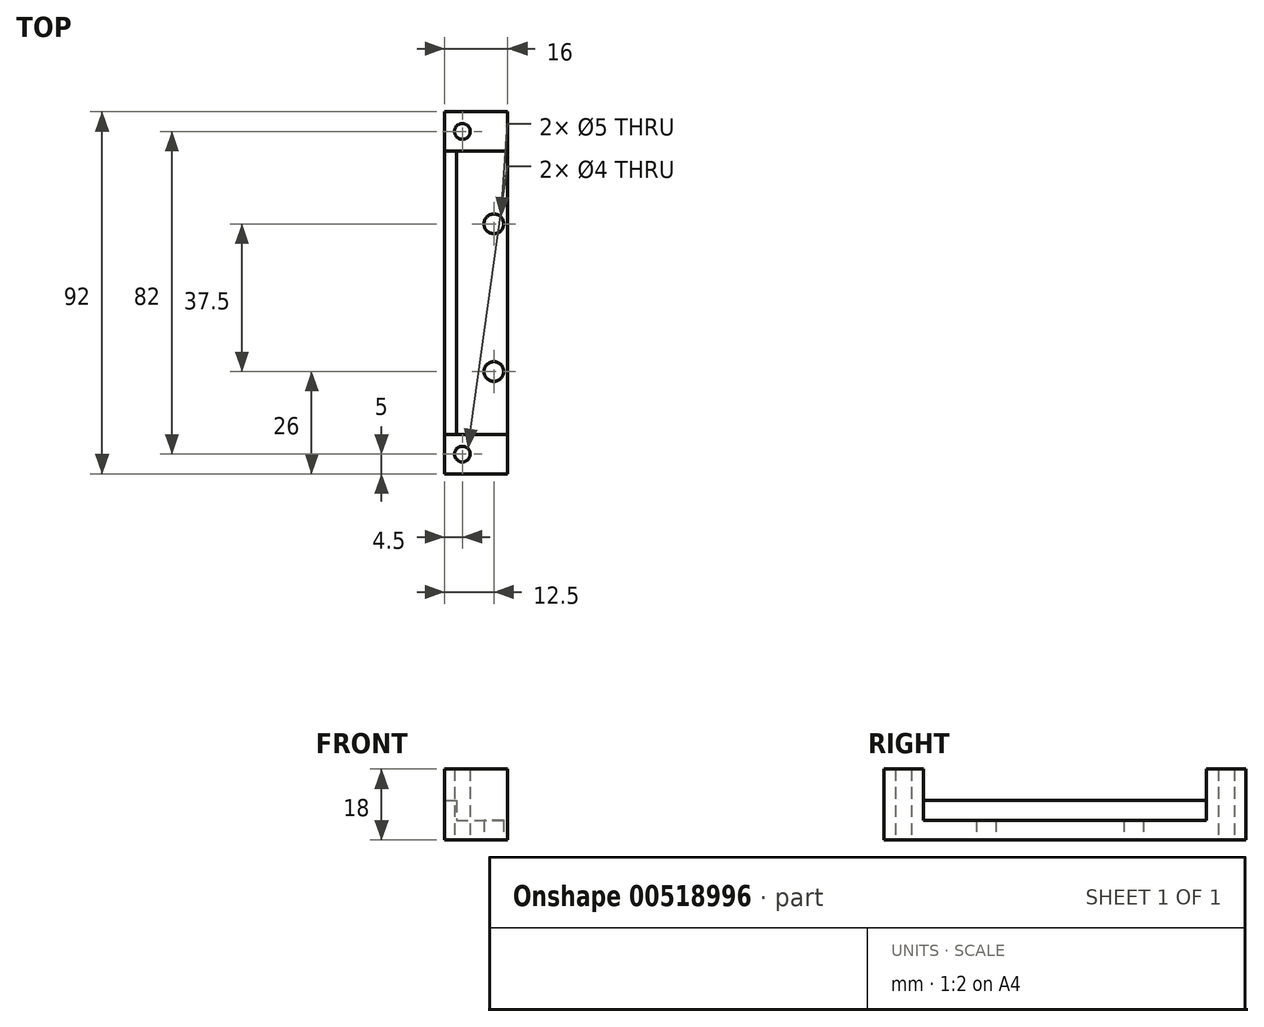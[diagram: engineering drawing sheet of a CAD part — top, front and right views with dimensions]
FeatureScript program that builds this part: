
annotation { "Feature Type Name" : "Feature", "Feature Type Description" : "" }
export const myFeature = defineFeature(function(context is Context, id is Id, definition is map)
    precondition{}
    {
        {
            var Q0;
            Q0=qCreatedBy(makeId("Top.planeOp"),FACE);
            var sketch = newSketch(context, id + "F0", { "sketchPlane" : qUnion([Q0])});
            skLineSegment(sketch, "E0.bottom", {"start": v(8, -46) * mm, "end": v(-8, -46) * mm});
            skLineSegment(sketch, "E0.top", {"start": v(8, 46) * mm, "end": v(-8, 46) * mm});
            skLineSegment(sketch, "E0.left", {"start": v(8, -46) * mm, "end": v(8, 46) * mm});
            skLineSegment(sketch, "E0.right", {"start": v(-8, -46) * mm, "end": v(-8, 46) * mm});
            skPoint(sketch, "E0.middle", {"position": v(0, 0) * mm});
            skCircle(sketch, "E1", {"center": v(4.5, 17.5) * mm, "radius": 2.5 * mm});
            skCircle(sketch, "E2", {"center": v(4.5, -20) * mm, "radius": 2.5 * mm});
            skLineSegment(sketch, "E3", {"start": v(4.5, 17.5) * mm, "end": v(4.5, 46) * mm, "construction": true});
            skLineSegment(sketch, "E4", {"start": v(4.5, -20) * mm, "end": v(4.5, -46) * mm, "construction": true});
            skCircle(sketch, "E5", {"center": v(-3.5, 41) * mm, "radius": 2 * mm, "construction": true});
            skCircle(sketch, "E6", {"center": v(-3.5, -41) * mm, "radius": 2 * mm, "construction": true});
            skLineSegment(sketch, "E7", {"start": v(-3.5, -41) * mm, "end": v(-8, -41) * mm, "construction": true});
            skLineSegment(sketch, "E8", {"start": v(-3.5, -41) * mm, "end": v(-3.5, -46) * mm, "construction": true});
            skLineSegment(sketch, "E9", {"start": v(-3.5, 41) * mm, "end": v(-3.5, 46) * mm, "construction": true});
            skSolve(sketch);
        }
        {
            var Q0;
            Q0=makeQuery(id+"F0.imprint","IMPRINT",FACE,{"disambiguationData":[TD([[makeQuery(id+"F0.imprint","IMPRINT",EDGE,{"derivedFrom":sQuery(id+"F0.wireOp",EDGE,"E0.bottom")}),-1.0]])]});
            extrude(context, id + "F1", {"entities" : qUnion([Q0]), "depth" : 5 * mm, "offsetDistance" : 25 * mm});
        }
        {
            var Q0;
            Q0=makeQuery(id+"F1.opExtrude","CAP_FACE",FACE,{"disambiguationData":[OSD([sQuery(id+"F0.wireOp",EDGE,"E0.bottom"),sQuery(id+"F0.wireOp",EDGE,"E0.top"),sQuery(id+"F0.wireOp",EDGE,"E0.left"),sQuery(id+"F0.wireOp",EDGE,"E0.right"),sQuery(id+"F0.wireOp",EDGE,"E1"),sQuery(id+"F0.wireOp",EDGE,"E2")])],"isStart":false});
            var sketch = newSketch(context, id + "F2", { "sketchPlane" : qUnion([Q0])});
            skLineSegment(sketch, "E10.bottom", {"start": v(-8, 46) * mm, "end": v(8, 46) * mm});
            skLineSegment(sketch, "E10.top", {"start": v(-8, 36) * mm, "end": v(8, 36) * mm});
            skLineSegment(sketch, "E10.left", {"start": v(-8, 46) * mm, "end": v(-8, 36) * mm});
            skLineSegment(sketch, "E10.right", {"start": v(8, 46) * mm, "end": v(8, 36) * mm});
            skLineSegment(sketch, "E11.bottom", {"start": v(-8, -46) * mm, "end": v(8, -46) * mm});
            skLineSegment(sketch, "E11.top", {"start": v(-8, -36) * mm, "end": v(8, -36) * mm});
            skLineSegment(sketch, "E11.left", {"start": v(-8, -46) * mm, "end": v(-8, -36) * mm});
            skLineSegment(sketch, "E11.right", {"start": v(8, -46) * mm, "end": v(8, -36) * mm});
            skLineSegment(sketch, "E12.bottom", {"start": v(-8, 36) * mm, "end": v(-5, 36) * mm});
            skLineSegment(sketch, "E12.top", {"start": v(-8, -36) * mm, "end": v(-5, -36) * mm});
            skLineSegment(sketch, "E12.left", {"start": v(-8, 36) * mm, "end": v(-8, -36) * mm});
            skLineSegment(sketch, "E12.right", {"start": v(-5, 36) * mm, "end": v(-5, -36) * mm});
            skSolve(sketch);
        }
        {
            var Q0;
            Q0=makeQuery(id+"F2.imprint","IMPRINT",FACE,{"disambiguationData":[TD([[makeQuery(id+"F2.imprint","IMPRINT",EDGE,{"derivedFrom":sQuery(id+"F2.wireOp",EDGE,"E11.bottom")}),-1.0]])]});
            var Q1;
            Q1=makeQuery(id+"F2.imprint","IMPRINT",FACE,{"disambiguationData":[TD([[makeQuery(id+"F2.imprint","IMPRINT",EDGE,{"derivedFrom":sQuery(id+"F2.wireOp",EDGE,"E10.bottom")}),1.0]])]});
            extrude(context, id + "F3", {"entities" : qUnion([Q0, Q1]), "operationType" : NewBodyOperationType.ADD, "depth" : 13 * mm, "offsetDistance" : 25 * mm});
        }
        {
            var Q0;
            Q0 = qSketchRegion(id + "F2", true);
            extrude(context, id + "F4", {"entities" : qUnion([Q0]), "operationType" : NewBodyOperationType.ADD, "depth" : 5 * mm, "offsetDistance" : 25 * mm});
        }
        {
            var Q0;
            Q0=makeQuery(id+"F1.opExtrude","CAP_FACE",FACE,{"disambiguationData":[OSD([sQuery(id+"F0.wireOp",EDGE,"E0.bottom"),sQuery(id+"F0.wireOp",EDGE,"E0.top"),sQuery(id+"F0.wireOp",EDGE,"E0.left"),sQuery(id+"F0.wireOp",EDGE,"E0.right"),sQuery(id+"F0.wireOp",EDGE,"E1"),sQuery(id+"F0.wireOp",EDGE,"E2")])],"isStart":true});
            var sketch = newSketch(context, id + "F5", { "sketchPlane" : qUnion([Q0])});
            skCircle(sketch, "E13", {"center": v(-3.5, -41) * mm, "radius": 2 * mm});
            skCircle(sketch, "E14", {"center": v(-3.5, 41) * mm, "radius": 2 * mm});
            skSolve(sketch);
        }
        {
            var Q0;
            Q0 = qSketchRegion(id + "F5", true);
            extrude(context, id + "F6", {"entities" : qUnion([Q0]), "operationType" : NewBodyOperationType.REMOVE, "oppositeDirection" : true, "depth" : 25 * mm, "offsetDistance" : 25 * mm});
        }
    });
